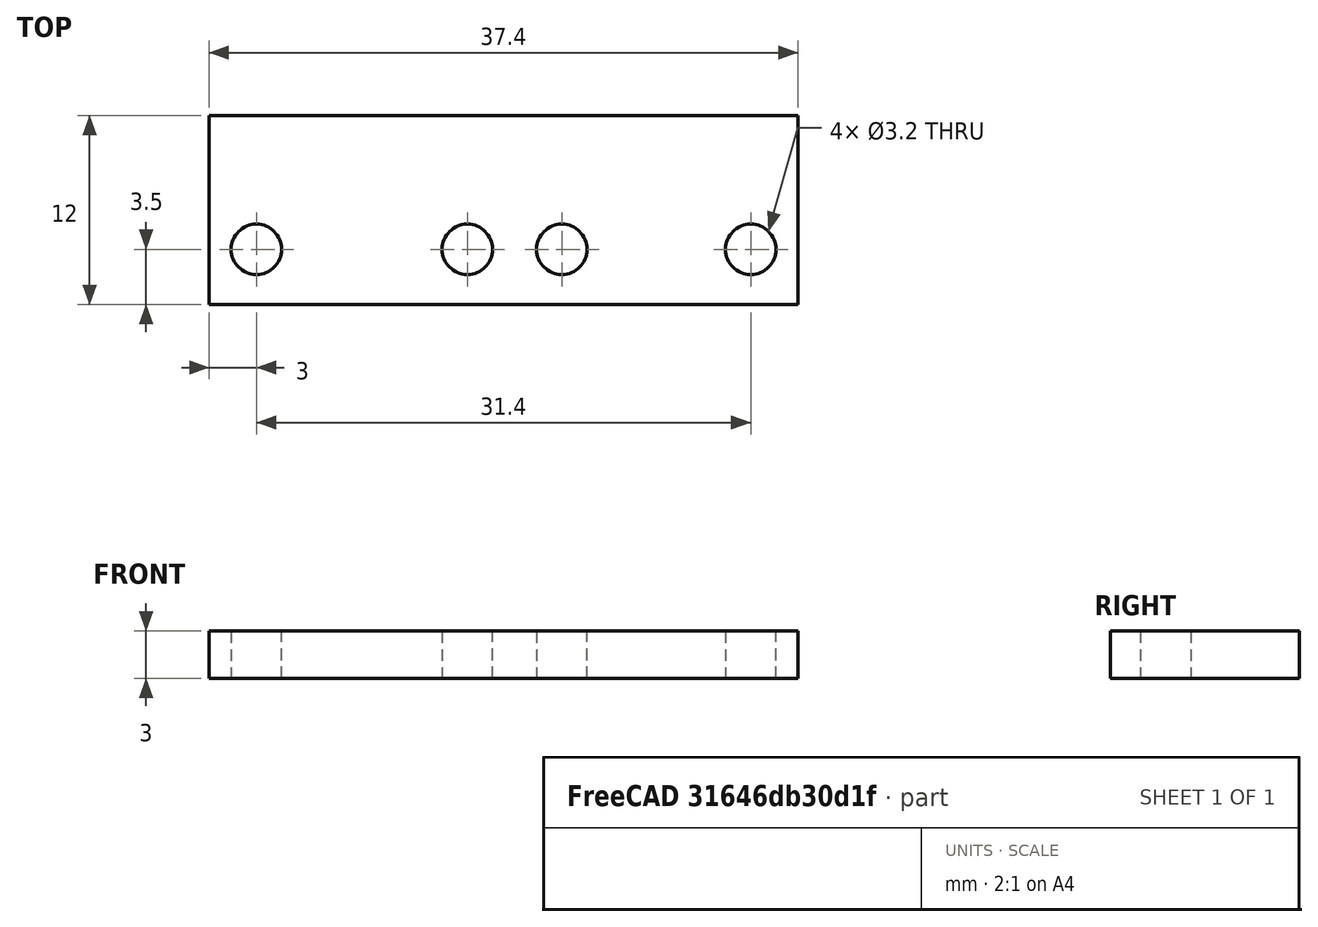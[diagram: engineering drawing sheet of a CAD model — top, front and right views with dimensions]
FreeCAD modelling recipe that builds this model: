
FCSTD DOCUMENT  (FreeCAD 0.19R24276 (Git))
Label: Endpoint_2_contact_holder
License: All rights reserved
LicenseURL: http://en.wikipedia.org/wiki/All_rights_reserved
objects: Sketcher::SketchObject×1, PartDesign::Pad×1, PartDesign::Body×1
note: 4 computed .brp shape members not serialized (recipe doc carries the construction recipe); baked Part::Feature solids carry a one-line shape summary decoded from their .brp

FEATURE [Sketcher::SketchObject] Sketch
  FullyConstrained = false
  MapMode = 5
  Support = -> [XY_Plane]
  sketch-geometry (13):
    g0: LineSegment StartX=0 StartY=0 StartZ=0 EndX=37.4 EndY=0 EndZ=0
    g1: LineSegment StartX=37.4 StartY=0 StartZ=0 EndX=37.4 EndY=7 EndZ=0
    g2: LineSegment StartX=37.4 StartY=7 StartZ=0 EndX=-4.15877 EndY=7 EndZ=0
    g3: LineSegment StartX=-2.07938 StartY=3.5 StartZ=0 EndX=65.2933 EndY=3.5 EndZ=0
    g4: Circle CenterX=3 CenterY=3.5 CenterZ=0 NormalX=0 NormalY=0 NormalZ=1 AngleXU=0 Radius=1.6
    g5: Circle CenterX=16.4 CenterY=3.5 CenterZ=0 NormalX=0 NormalY=0 NormalZ=1 AngleXU=0 Radius=1.6
    g6: LineSegment StartX=19.4 StartY=7 StartZ=0 EndX=19.4 EndY=0 EndZ=0
    g7: LineSegment StartX=28.4 StartY=7 StartZ=0 EndX=28.4 EndY=0 EndZ=0
    g8: Circle CenterX=22.4 CenterY=3.5 CenterZ=0 NormalX=0 NormalY=0 NormalZ=1 AngleXU=0 Radius=1.6
    g9: Circle CenterX=34.4 CenterY=3.5 CenterZ=0 NormalX=0 NormalY=0 NormalZ=1 AngleXU=0 Radius=1.6
    g10: LineSegment StartX=0 StartY=0 StartZ=0 EndX=0 EndY=12 EndZ=0
    g11: LineSegment StartX=0 StartY=12 StartZ=0 EndX=37.4 EndY=12 EndZ=0
    g12: LineSegment StartX=37.4 StartY=0 StartZ=0 EndX=37.4 EndY=12 EndZ=0
  constraints (37):
    c: Coincident(g0,g1)
    c: Coincident(g1,g2)
    c: Horizontal(g0)
    c: Horizontal(g2)
    c: Vertical(g1)
    c: Coincident(g0,g-1)
    c: DistanceY(g0,g2) = 7
    c: Horizontal(g3)
    c: Symmetric(g2,g-1,g3)
    c: PointOnObject(g4,g3)
    c: PointOnObject(g5,g3)
    c: DistanceX(g-1,g4) = 3
    c: DistanceX(g4,g5) = 13.4
    c: Vertical(g6)
    c: PointOnObject(g6,g2)
    c: PointOnObject(g6,g0)
    c: DistanceX(g5,g6) = 3
    c: DistanceX(g6,g0) = 18
    c: Vertical(g7)
    c: Symmetric(g6,g1,g7)
    c: PointOnObject(g7,g0)
    c: PointOnObject(g8,g3)
    c: PointOnObject(g9,g3)
    c: DistanceX(g8,g7) = 6
    c: DistanceX(g7,g9) = 6
    c: Diameter(g8) = 3.2
    c: Equal(g8,g9)
    c: Equal(g8,g5)
    c: Equal(g8,g4)
    c: Coincident(g10,g0)
    c: PointOnObject(g10,g-2)
    c: DistanceY(g10,g10) = 12
    c: Coincident(g11,g10)
    c: Horizontal(g11)
    c: Coincident(g12,g0)
    c: Vertical(g12)
    c: Coincident(g12,g11)
FEATURE [PartDesign::Pad] Pad
  Direction = (1,1,1)
  Length = 3
  Length2 = 100
  Profile = -> Sketch
  Type = 0
FEATURE [PartDesign::Body] Body
  Group = -> [Sketch,Pad]
  Origin = -> Origin
  Tip = -> Pad
